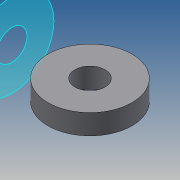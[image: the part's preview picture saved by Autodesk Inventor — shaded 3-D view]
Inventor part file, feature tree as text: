
AUTODESK INVENTOR PART (.ipt)
format: ipt  version: 2017 (Build 210142000, 142)  size: 81,408 bytes
history: native  units: mm
features: other x1, extrude x1, sketch x1
ambient origin geometry x8: Origin, YZ Plane, XZ Plane, XY Plane, X Axis, Y Axis, Z Axis, Center Point
bodies: Body1 (feature_tree)
feature tree (3):
  other  "Sólido1"
  extrude  "Extrusión1"  Depth=6.0mm
  sketch  "Boceto1"  dims[d0=8.0mm d1=9.0mm d2=6.0mm d3=0.0mm]
